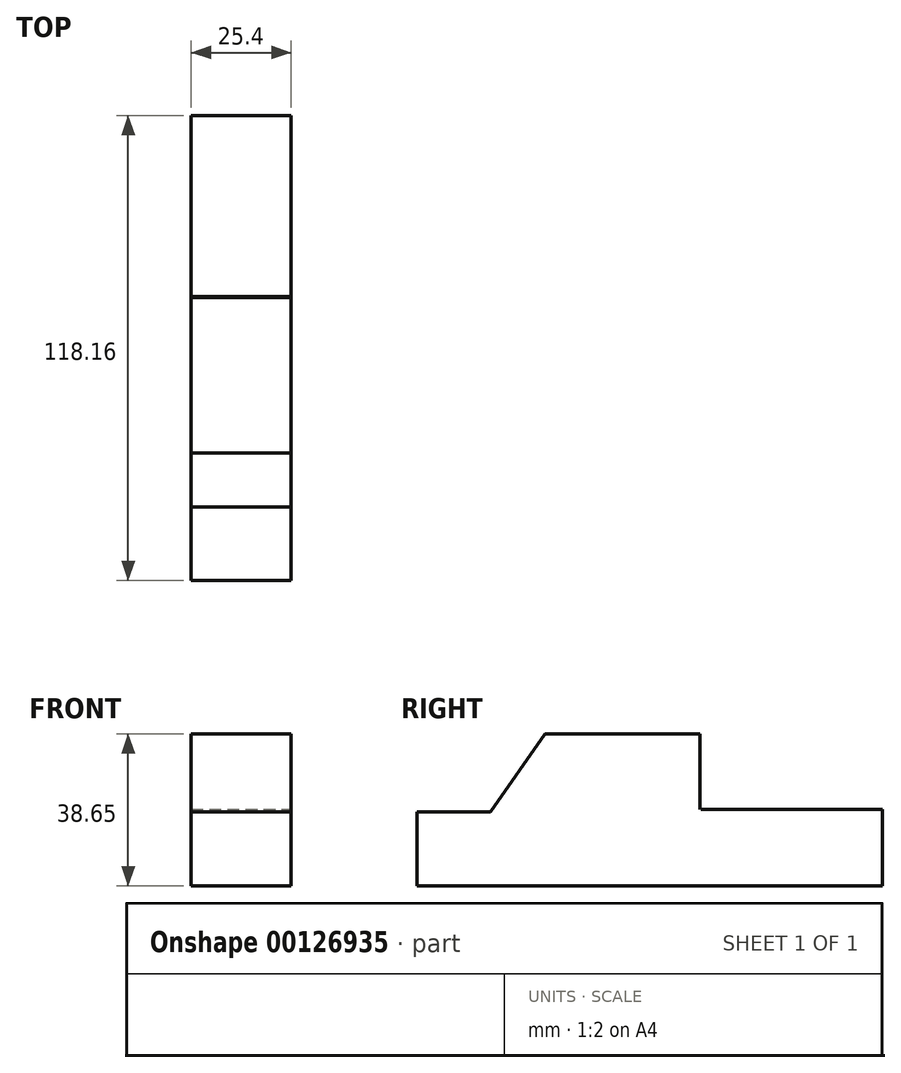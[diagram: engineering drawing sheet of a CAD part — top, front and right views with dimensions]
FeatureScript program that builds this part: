
annotation { "Feature Type Name" : "Feature", "Feature Type Description" : "" }
export const myFeature = defineFeature(function(context is Context, id is Id, definition is map)
    precondition{}
    {
        {
            var Q0;
            Q0=qCreatedBy(makeId("Right.planeOp"),FACE);
            var sketch = newSketch(context, id + "F0", { "sketchPlane" : qUnion([Q0])});
            skLineSegment(sketch, "E0", {"start": v(0, 24.93) * mm, "end": v(-39.45, 24.93) * mm});
            skLineSegment(sketch, "E1", {"start": v(-39.45, 24.93) * mm, "end": v(-53.27, 5.1) * mm});
            skLineSegment(sketch, "E2", {"start": v(-53.27, 5.1) * mm, "end": v(-71.9, 5.1) * mm});
            skLineSegment(sketch, "E3", {"start": v(-71.9, 5.1) * mm, "end": v(-71.9, -13.72) * mm});
            skLineSegment(sketch, "E4", {"start": v(-71.9, -13.72) * mm, "end": v(0, -13.72) * mm});
            skLineSegment(sketch, "E5", {"start": v(0, 24.93) * mm, "end": v(0, 5.7) * mm});
            skLineSegment(sketch, "E6", {"start": v(0.2, 5.7) * mm, "end": v(46.26, 5.7) * mm});
            skLineSegment(sketch, "E7", {"start": v(0, -13.72) * mm, "end": v(46.26, -13.72) * mm});
            skLineSegment(sketch, "E8", {"start": v(46.26, 5.7) * mm, "end": v(46.26, -13.72) * mm});
            skSolve(sketch);
        }
        {
            var Q0;
            Q0=sQuery(id+"F0.wireOp",EDGE,"E0");
            var Q1;
            Q1=sQuery(id+"F0.wireOp",EDGE,"E1");
            var Q2;
            Q2=sQuery(id+"F0.wireOp",EDGE,"E5");
            var Q3;
            Q3=sQuery(id+"F0.wireOp",EDGE,"E6");
            var Q4;
            Q4=sQuery(id+"F0.wireOp",EDGE,"E8");
            var Q5;
            Q5=sQuery(id+"F0.wireOp",EDGE,"E7");
            var Q6;
            Q6=sQuery(id+"F0.wireOp",EDGE,"E4");
            var Q7;
            Q7=sQuery(id+"F0.wireOp",EDGE,"E3");
            var Q8;
            Q8=sQuery(id+"F0.wireOp",EDGE,"E2");
            extrude(context, id + "F1", {"bodyType" : ToolBodyType.SURFACE, "surfaceEntities" : qUnion([Q0, Q1, Q2, Q3, Q4, Q5, Q6, Q7, Q8]), "depth" : 25.4 * mm});
        }
    });
